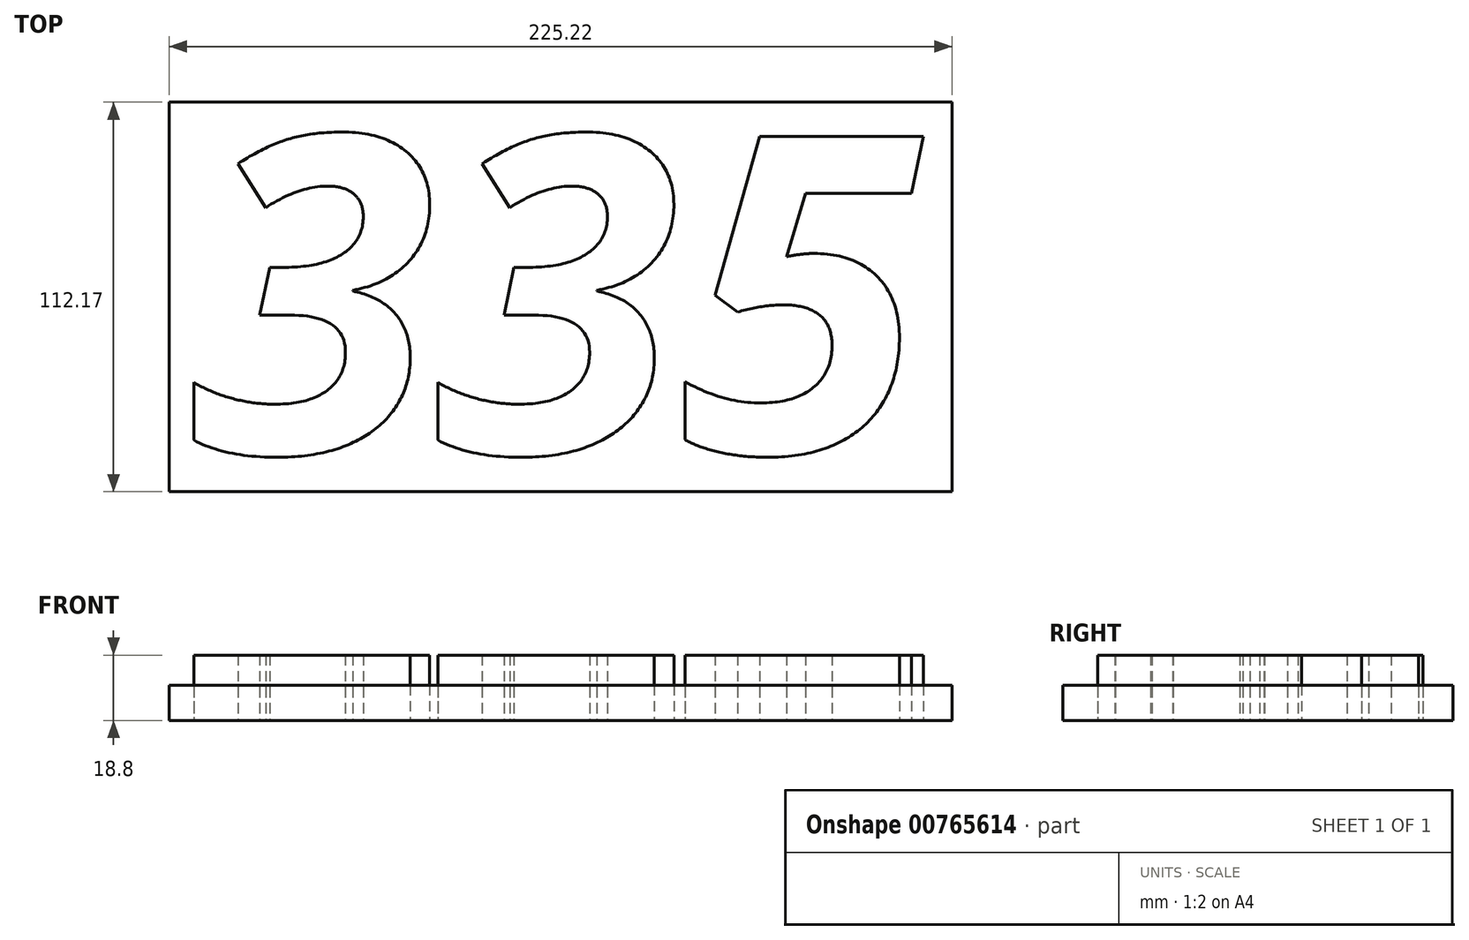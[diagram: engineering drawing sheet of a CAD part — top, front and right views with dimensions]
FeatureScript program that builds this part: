
annotation { "Feature Type Name" : "Feature", "Feature Type Description" : "" }
export const myFeature = defineFeature(function(context is Context, id is Id, definition is map)
    precondition{}
    {
        {
            var Q0;
            Q0=qCreatedBy(makeId("Top.planeOp"),FACE);
            var sketch = newSketch(context, id + "F0", { "sketchPlane" : qUnion([Q0])});
            skText(sketch, "E0", { "text": "335", "fontName": "OpenSans-BoldItalic.ttf"});
            const initialGuessF0  = {"E0": [-0.09419, -0.04437, 1, 0, 0.09185]};
            skSetInitialGuess(sketch, initialGuessF0);
            skSolve(sketch);
        }
        {
            var Q0;
            Q0=makeQuery(id+"F0.imprint","IMPRINT",FACE,{"disambiguationData":[TD([[makeQuery(id+"F0.imprint","IMPRINT",EDGE,{"derivedFrom":sQuery(id+"F0.wireOp",EDGE,"E0.sketch_text.stroke-0")}),-1.0]])]});
            var Q1;
            Q1=makeQuery(id+"F0.imprint","IMPRINT",FACE,{"disambiguationData":[TD([[makeQuery(id+"F0.imprint","IMPRINT",EDGE,{"derivedFrom":sQuery(id+"F0.wireOp",EDGE,"E0.sketch_text.stroke-28")}),-1.0]])]});
            var Q2;
            Q2=makeQuery(id+"F0.imprint","IMPRINT",FACE,{"disambiguationData":[TD([[makeQuery(id+"F0.imprint","IMPRINT",EDGE,{"derivedFrom":sQuery(id+"F0.wireOp",EDGE,"E0.sketch_text.stroke-56")}),-1.0]])]});
            extrude(context, id + "F1", {"entities" : qUnion([Q0, Q1, Q2]), "depth" : 18.8 * mm, "offsetDistance" : 25.4 * mm});
        }
        {
            var Q0;
            Q0=qCreatedBy(makeId("Top.planeOp"),FACE);
            var sketch = newSketch(context, id + "F2", { "sketchPlane" : qUnion([Q0])});
            skLineSegment(sketch, "E1.bottom", {"start": v(-100.37, 56.6) * mm, "end": v(124.85, 56.6) * mm});
            skLineSegment(sketch, "E1.top", {"start": v(-100.37, -55.56) * mm, "end": v(124.85, -55.56) * mm});
            skLineSegment(sketch, "E1.left", {"start": v(-100.37, 56.6) * mm, "end": v(-100.37, -55.56) * mm});
            skLineSegment(sketch, "E1.right", {"start": v(124.85, 56.6) * mm, "end": v(124.85, -55.56) * mm});
            skSolve(sketch);
        }
        {
            var Q0;
            Q0=makeQuery(id+"F2.imprint","IMPRINT",FACE,{"disambiguationData":[TD([[makeQuery(id+"F2.imprint","IMPRINT",EDGE,{"derivedFrom":sQuery(id+"F2.wireOp",EDGE,"E1.bottom")}),-1.0]])]});
            extrude(context, id + "F3", {"entities" : qUnion([Q0]), "depth" : 10.16 * mm, "offsetDistance" : 25.4 * mm});
        }
    });
